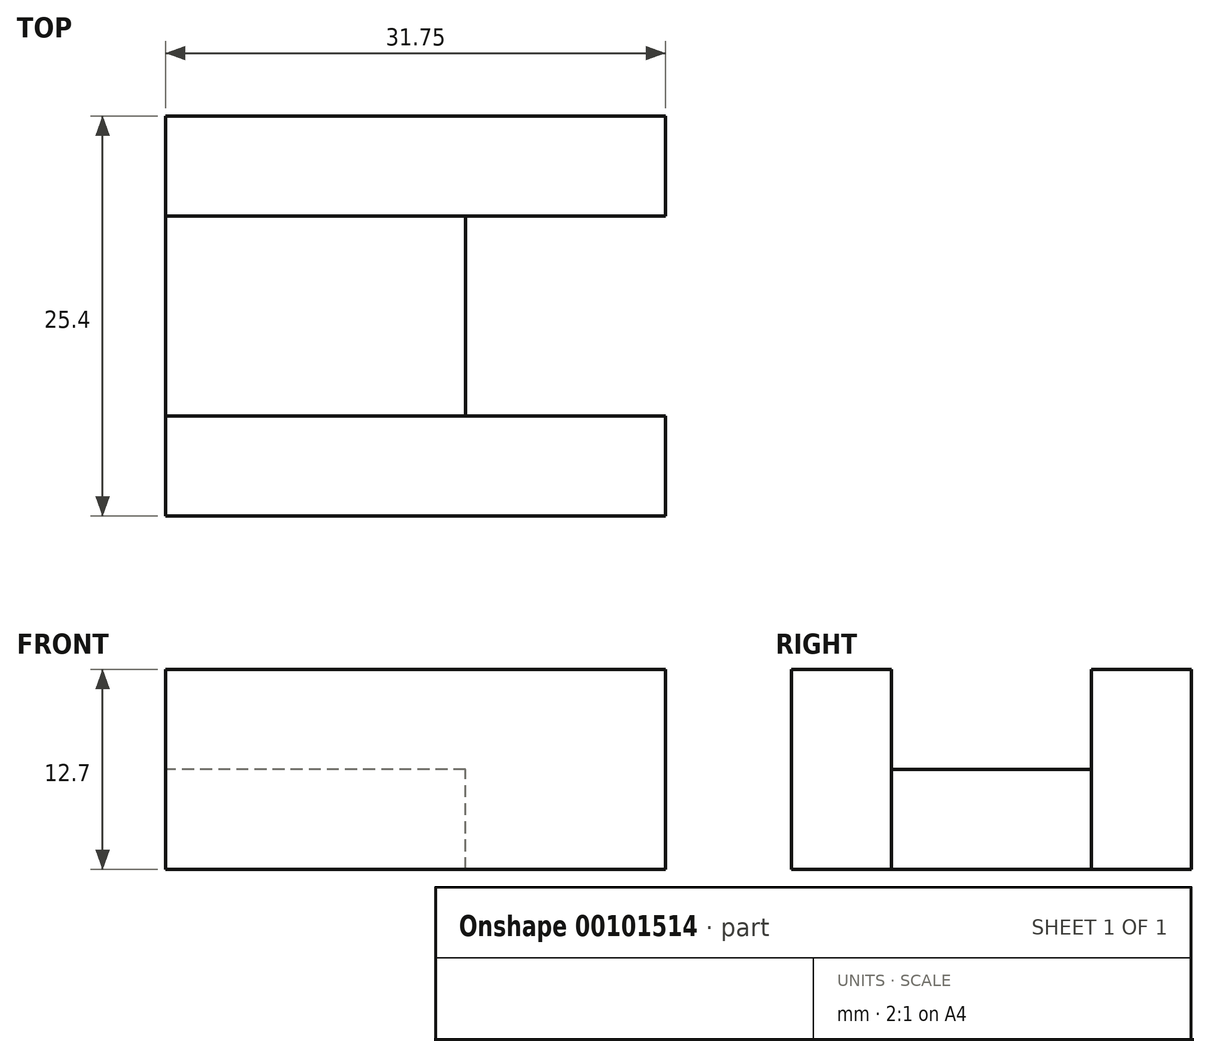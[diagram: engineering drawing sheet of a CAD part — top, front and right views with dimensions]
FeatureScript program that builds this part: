
annotation { "Feature Type Name" : "Feature", "Feature Type Description" : "" }
export const myFeature = defineFeature(function(context is Context, id is Id, definition is map)
    precondition{}
    {
        {
            var Q0;
            Q0=qCreatedBy(makeId("Front.planeOp"),FACE);
            var sketch = newSketch(context, id + "F0", { "sketchPlane" : qUnion([Q0])});
            skLineSegment(sketch, "E0.bottom", {"start": v(0, 0) * mm, "end": v(38.1, 0) * mm});
            skLineSegment(sketch, "E0.top", {"start": v(0, -25.4) * mm, "end": v(38.1, -25.4) * mm});
            skLineSegment(sketch, "E0.left", {"start": v(0, 0) * mm, "end": v(0, -25.4) * mm});
            skLineSegment(sketch, "E0.right", {"start": v(38.1, 0) * mm, "end": v(38.1, -25.4) * mm});
            skPoint(sketch, "E1.oppositeSnap0", {"position": v(38.1, -12.7) * mm});
            skLineSegment(sketch, "E1.bottom", {"start": v(38.1, 0) * mm, "end": v(6.35, 0) * mm});
            skLineSegment(sketch, "E1.top", {"start": v(38.1, -12.7) * mm, "end": v(6.35, -12.7) * mm});
            skLineSegment(sketch, "E1.left", {"start": v(38.1, 0) * mm, "end": v(38.1, -12.7) * mm});
            skLineSegment(sketch, "E1.right", {"start": v(6.35, 0) * mm, "end": v(6.35, -12.7) * mm});
            skSolve(sketch);
        }
        {
            var Q0;
            Q0=makeQuery(id+"F0.imprint","IMPRINT",FACE,{"disambiguationData":[TD([[makeQuery(id+"F0.imprint","IMPRINT",EDGE,{"derivedFrom":sQuery(id+"F0.wireOp",EDGE,"E0.bottom")}),-1.0]])]});
            extrude(context, id + "F1", {"entities" : qUnion([Q0]), "depth" : 25.4 * mm});
        }
        {
            var Q0;
            Q0=qCreatedBy(makeId("Right.planeOp"),FACE);
            var sketch = newSketch(context, id + "F2", { "sketchPlane" : qUnion([Q0])});
            skLineSegment(sketch, "E2.bottom", {"start": v(0, 0) * mm, "end": v(-6.35, 0) * mm});
            skLineSegment(sketch, "E2.top", {"start": v(0, -9.9) * mm, "end": v(-6.35, -9.9) * mm});
            skLineSegment(sketch, "E2.left", {"start": v(0, 0) * mm, "end": v(0, -9.9) * mm});
            skLineSegment(sketch, "E2.right", {"start": v(-6.35, 0) * mm, "end": v(-6.35, -9.9) * mm});
            skLineSegment(sketch, "E3.bottom", {"start": v(-6.35, 0) * mm, "end": v(-19.05, 0) * mm});
            skLineSegment(sketch, "E3.top", {"start": v(-6.35, -6.35) * mm, "end": v(-19.05, -6.35) * mm});
            skLineSegment(sketch, "E3.left", {"start": v(-6.35, 0) * mm, "end": v(-6.35, -6.35) * mm});
            skLineSegment(sketch, "E3.right", {"start": v(-19.05, 0) * mm, "end": v(-19.05, -6.35) * mm});
            skSolve(sketch);
        }
        {
            var Q0;
            Q0=makeQuery(id+"F2.imprint","IMPRINT",FACE,{"disambiguationData":[TD([[makeQuery(id+"F2.imprint","IMPRINT",EDGE,{"derivedFrom":sQuery(id+"F2.wireOp",EDGE,"E3.bottom")}),1.0]])]});
            extrude(context, id + "F3", {"entities" : qUnion([Q0]), "operationType" : NewBodyOperationType.REMOVE, "depth" : 25.4 * mm});
        }
        {
            var Q0;
            Q0=qCreatedBy(makeId("Top.planeOp"),FACE);
            var sketch = newSketch(context, id + "F4", { "sketchPlane" : qUnion([Q0])});
            skLineSegment(sketch, "E4.bottom", {"start": v(0, 0) * mm, "end": v(25.4, 0) * mm});
            skLineSegment(sketch, "E4.top", {"start": v(0, -6.35) * mm, "end": v(25.4, -6.35) * mm});
            skLineSegment(sketch, "E4.left", {"start": v(0, 0) * mm, "end": v(0, -6.35) * mm});
            skLineSegment(sketch, "E4.right", {"start": v(25.4, 0) * mm, "end": v(25.4, -6.35) * mm});
            skLineSegment(sketch, "E5.bottom", {"start": v(25.4, -6.35) * mm, "end": v(38.1, -6.35) * mm});
            skLineSegment(sketch, "E5.top", {"start": v(25.4, -19.05) * mm, "end": v(38.1, -19.05) * mm});
            skLineSegment(sketch, "E5.left", {"start": v(25.4, -6.35) * mm, "end": v(25.4, -19.05) * mm});
            skLineSegment(sketch, "E5.right", {"start": v(38.1, -6.35) * mm, "end": v(38.1, -19.05) * mm});
            skSolve(sketch);
        }
        {
            var Q0;
            Q0=makeQuery(id+"F4.imprint","IMPRINT",FACE,{"disambiguationData":[TD([[makeQuery(id+"F4.imprint","IMPRINT",EDGE,{"derivedFrom":sQuery(id+"F4.wireOp",EDGE,"E5.bottom")}),-1.0]])]});
            extrude(context, id + "F5", {"entities" : qUnion([Q0]), "operationType" : NewBodyOperationType.REMOVE, "endBound" : BoundingType.THROUGH_ALL, "oppositeDirection" : true, "depth" : 25.4 * mm});
        }
    });
